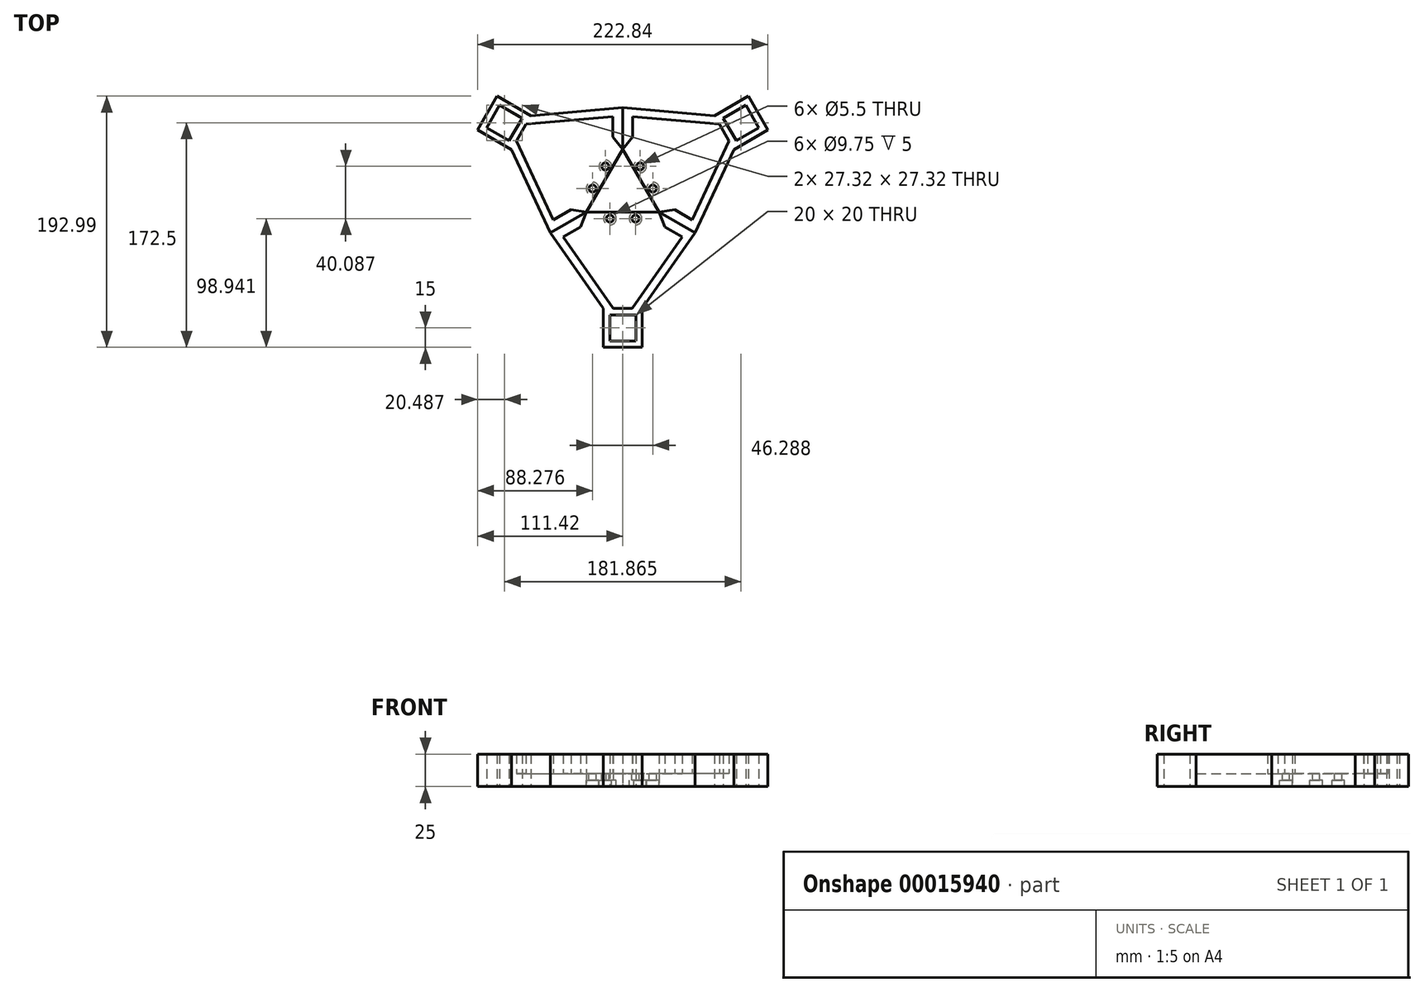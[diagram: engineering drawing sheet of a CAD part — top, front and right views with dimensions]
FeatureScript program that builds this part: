
annotation { "Feature Type Name" : "Feature", "Feature Type Description" : "" }
export const myFeature = defineFeature(function(context is Context, id is Id, definition is map)
    precondition{}
    {
        {
            var Q0;
            Q0=qCreatedBy(makeId("Top.planeOp"),FACE);
            var sketch = newSketch(context, id + "F0", { "sketchPlane" : qUnion([Q0])});
            skLineSegment(sketch, "E0", {"start": v(-55.56, -32.08) * mm, "end": v(-27.82, -16.06) * mm});
            skLineSegment(sketch, "E1", {"start": v(55.56, -32.08) * mm, "end": v(27.82, -16.06) * mm});
            skPoint(sketch, "E2", {"position": v(0, -120) * mm});
            skLineSegment(sketch, "E3", {"start": v(-27.82, -16.06) * mm, "end": v(27.82, -16.06) * mm});
            skLineSegment(sketch, "E4", {"start": v(-15, -120) * mm, "end": v(15, -120) * mm});
            skLineSegment(sketch, "E5", {"start": v(15, -120) * mm, "end": v(15, -90) * mm});
            skLineSegment(sketch, "E6", {"start": v(-15, -120) * mm, "end": v(-15, -90) * mm});
            skLineSegment(sketch, "E7", {"start": v(-15, -90) * mm, "end": v(-55.56, -32.08) * mm});
            skLineSegment(sketch, "E8", {"start": v(15, -90) * mm, "end": v(55.56, -32.08) * mm});
            skPoint(sketch, "E9.center.orphan", {"position": v(0, 0) * mm});
            skPoint(sketch, "E10", {"position": v(15, -105) * mm});
            skPoint(sketch, "E11", {"position": v(0, -105) * mm});
            skLineSegment(sketch, "E12.bottom", {"start": v(10, -95) * mm, "end": v(-10, -95) * mm});
            skLineSegment(sketch, "E12.top", {"start": v(10, -115) * mm, "end": v(-10, -115) * mm});
            skLineSegment(sketch, "E12.left", {"start": v(10, -95) * mm, "end": v(10, -115) * mm});
            skLineSegment(sketch, "E12.right", {"start": v(-10, -95) * mm, "end": v(-10, -115) * mm});
            skLineSegment(sketch, "E13", {"start": v(-15, -90) * mm, "end": v(15, -90) * mm});
            skLineSegment(sketch, "E14", {"start": v(-7.45, -90) * mm, "end": v(-45.85, -35.16) * mm});
            skLineSegment(sketch, "E15", {"start": v(-45.85, -35.16) * mm, "end": v(-32.33, -27.35) * mm});
            skLineSegment(sketch, "E16", {"start": v(-32.33, -27.35) * mm, "end": v(-27.82, -16.06) * mm});
            skLineSegment(sketch, "E17", {"start": v(-45.85, -35.16) * mm, "end": v(-51.23, -38.26) * mm, "construction": true});
            skLineSegment(sketch, "E18.MirrorCS", {"start": v(32.33, -27.35) * mm, "end": v(27.82, -16.06) * mm});
            skLineSegment(sketch, "E19.MirrorCS", {"start": v(7.45, -90) * mm, "end": v(45.85, -35.16) * mm});
            skLineSegment(sketch, "E20.MirrorCS", {"start": v(45.85, -35.16) * mm, "end": v(32.33, -27.35) * mm});
            skLineSegment(sketch, "E21", {"start": v(0, -90) * mm, "end": v(0, -90) * mm});
            skLineSegment(sketch, "E22", {"start": v(0, 0) * mm, "end": v(0, -90) * mm, "construction": true});
            skPoint(sketch, "E23", {"position": v(9.81, -21.06) * mm});
            skPoint(sketch, "E24.MirrorP", {"position": v(-9.81, -21.06) * mm});
            skLineSegment(sketch, "E25", {"start": v(9.81, -21.06) * mm, "end": v(9.81, -16.06) * mm, "construction": true});
            skLineSegment(sketch, "E26", {"start": v(9.81, -21.06) * mm, "end": v(29.81, -21.06) * mm, "construction": true});
            skSolve(sketch);
        }
        {
            var Q0;
            Q0=qCreatedBy(makeId("Front.planeOp"),FACE);
            var sketch = newSketch(context, id + "F1", { "sketchPlane" : qUnion([Q0])});
            skLineSegment(sketch, "E27", {"start": v(0, 0) * mm, "end": v(0, 121.57) * mm, "construction": true});
            skSolve(sketch);
        }
        {
            var Q0;
            Q0=makeQuery(id+"F0.imprint","IMPRINT",FACE,{"disambiguationData":[TD([[makeQuery(id+"F0.imprint","IMPRINT",EDGE,{"derivedFrom":sQuery(id+"F0.wireOp",EDGE,"E0")}),-1.0]])]});
            var Q1;
            {var subQ3=sQuery(id+"F0.wireOp",EDGE,"E1");Q1=makeQuery(id+"F0.imprint","IMPRINT",FACE,{"disambiguationData":[TD([[makeQuery(id+"F0.imprint","IMPRINT",EDGE,{"derivedFrom":subQ3}),1.0]])]});}
            var Q2;
            Q2=makeQuery(id+"F0.imprint","IMPRINT",FACE,{"disambiguationData":[TD([[makeQuery(id+"F0.imprint","IMPRINT",EDGE,{"derivedFrom":sQuery(id+"F0.wireOp",EDGE,"E4")}),1.0]])]});
            extrude(context, id + "F2", {"entities" : qUnion([Q0, Q1, Q2]), "depth" : 25 * mm});
        }
        {
            var Q0;
            {var subQ0=sQuery(id+"F0.wireOp",EDGE,"E14");Q0=makeQuery(id+"F0.imprint","IMPRINT",FACE,{"disambiguationData":[TD([[makeQuery(id+"F0.imprint","IMPRINT",EDGE,{"derivedFrom":subQ0}),-1.0]])]});}
            extrude(context, id + "F3", {"entities" : qUnion([Q0]), "operationType" : NewBodyOperationType.ADD, "depth" : 10 * mm});
        }
        {
            var Q0;
            Q0=sQuery(id+"F0.wireOp",VERTEX,"E23");
            var Q1;
            Q1=sQuery(id+"F0.wireOp",VERTEX,"E24.MirrorP");
            var Q2;
            Q2=makeQuery(id+"F2.opExtrude","SWEPT_BODY",BODY,{"disambiguationData":[OSD([sQuery(id+"F0.wireOp",EDGE,"E0"),sQuery(id+"F0.wireOp",EDGE,"E1"),sQuery(id+"F0.wireOp",EDGE,"E4"),sQuery(id+"F0.wireOp",EDGE,"E5"),sQuery(id+"F0.wireOp",EDGE,"E6"),sQuery(id+"F0.wireOp",EDGE,"E7"),sQuery(id+"F0.wireOp",EDGE,"E8"),sQuery(id+"F0.wireOp",EDGE,"E12.bottom"),sQuery(id+"F0.wireOp",EDGE,"E12.top"),sQuery(id+"F0.wireOp",EDGE,"E12.left"),sQuery(id+"F0.wireOp",EDGE,"E12.right"),sQuery(id+"F0.wireOp",EDGE,"E13"),sQuery(id+"F0.wireOp",EDGE,"E14"),sQuery(id+"F0.wireOp",EDGE,"E15"),sQuery(id+"F0.wireOp",EDGE,"E16"),sQuery(id+"F0.wireOp",EDGE,"E18.MirrorCS"),sQuery(id+"F0.wireOp",EDGE,"E19.MirrorCS"),sQuery(id+"F0.wireOp",EDGE,"E20.MirrorCS")])]});
            hole(context, id + "F4", {"style" : HoleStyle.C_BORE, "endStyle" : HoleEndStyle.THROUGH, "oppositeDirection" : true, "standardTappedOrClearance" : lookupTablePath({ "standard" : "ISO", "fit" : "Normal", "size" : "M5", "type" : "Clearance" }), "standardBlindInLast" : lookupTablePath({ "fit" : "Standard", "standard" : "ISO", "size" : "M5", "type" : "Clearance" }), "holeDiameter" : 5.5 * mm, "cBoreDiameter" : 9.75 * mm, "cBoreDepth" : 5 * mm, "locations" : qUnion([Q0, Q1]), "scope" : qUnion([Q2]), "isTappedThrough" : true, "startStyle" : HoleStartStyle.PART});
        }
        {
            var Q0;
            Q0=makeQuery(id+"F2.opExtrude","SWEPT_BODY",BODY,{"disambiguationData":[OSD([sQuery(id+"F0.wireOp",EDGE,"E0"),sQuery(id+"F0.wireOp",EDGE,"E1"),sQuery(id+"F0.wireOp",EDGE,"E3"),sQuery(id+"F0.wireOp",EDGE,"E4"),sQuery(id+"F0.wireOp",EDGE,"E5"),sQuery(id+"F0.wireOp",EDGE,"E6"),sQuery(id+"F0.wireOp",EDGE,"E7"),sQuery(id+"F0.wireOp",EDGE,"E8"),sQuery(id+"F0.wireOp",EDGE,"E12.bottom"),sQuery(id+"F0.wireOp",EDGE,"E12.top"),sQuery(id+"F0.wireOp",EDGE,"E12.left"),sQuery(id+"F0.wireOp",EDGE,"E12.right"),sQuery(id+"F0.wireOp",EDGE,"E13"),sQuery(id+"F0.wireOp",EDGE,"E14"),sQuery(id+"F0.wireOp",EDGE,"E15"),sQuery(id+"F0.wireOp",EDGE,"E16"),sQuery(id+"F0.wireOp",EDGE,"E18.MirrorCS"),sQuery(id+"F0.wireOp",EDGE,"E19.MirrorCS"),sQuery(id+"F0.wireOp",EDGE,"E20.MirrorCS")])]});
            var Q1;
            Q1=sQuery(id+"F1.wireOp",EDGE,"E27");
            circularPattern(context, id + "F5", {"entities" : qUnion([Q0]), "axis" : qUnion([Q1]), "angle" : 120 * degree, "instanceCount" : 3});
        }
    });
